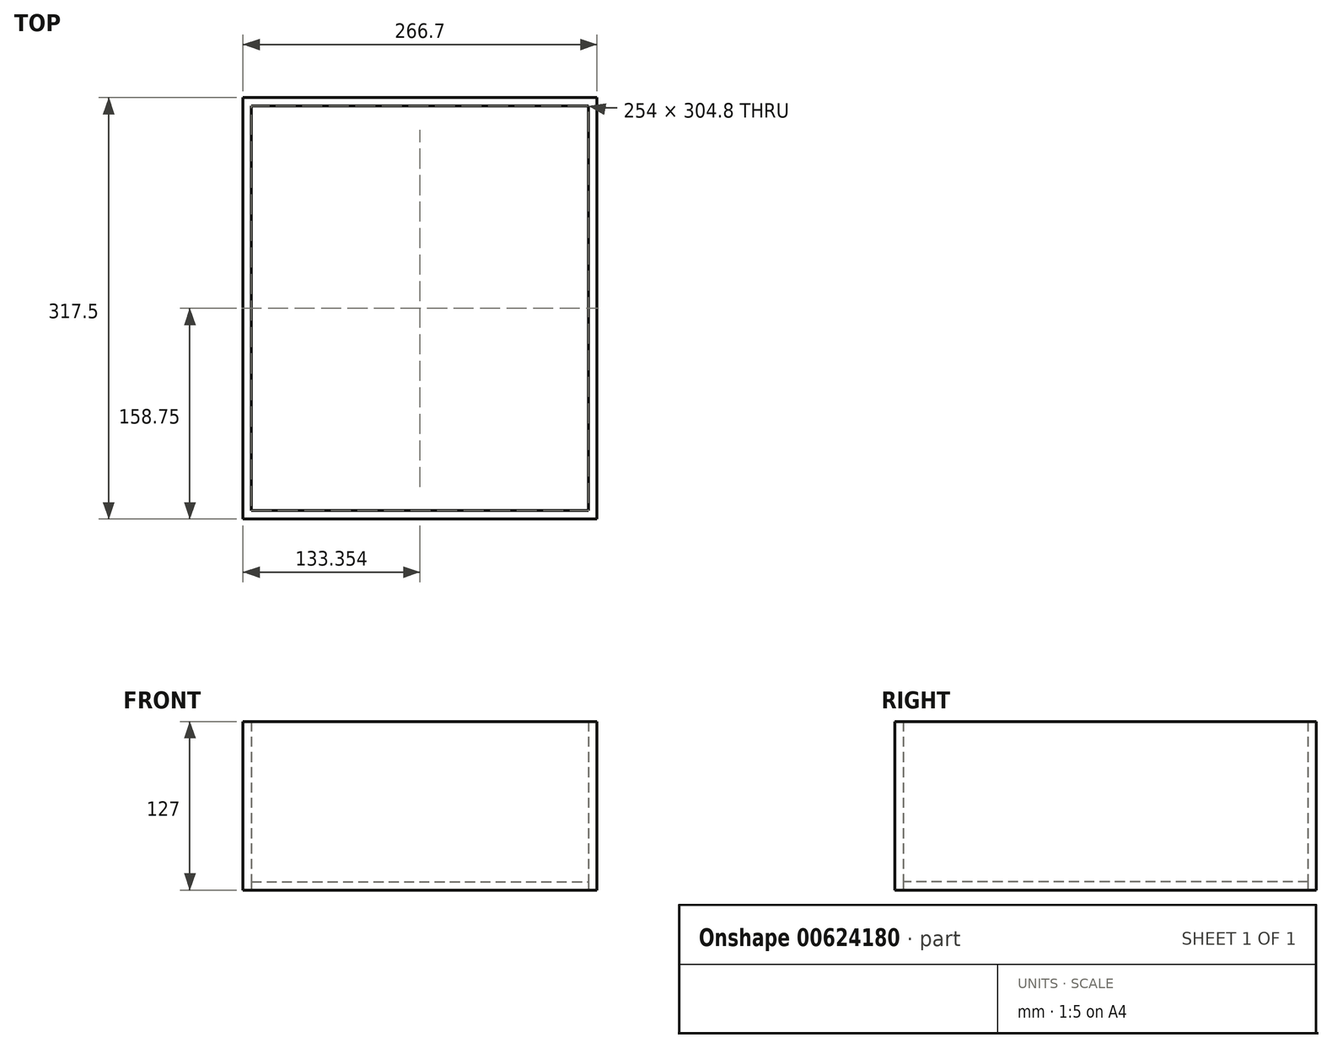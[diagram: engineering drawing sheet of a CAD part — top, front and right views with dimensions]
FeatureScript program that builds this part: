
annotation { "Feature Type Name" : "Feature", "Feature Type Description" : "" }
export const myFeature = defineFeature(function(context is Context, id is Id, definition is map)
    precondition{}
    {
        {
            var Q0;
            Q0=qCreatedBy(makeId("Top.planeOp"),FACE);
            var sketch = newSketch(context, id + "F0", { "sketchPlane" : qUnion([Q0])});
            skLineSegment(sketch, "E0.bottom", {"start": v(-126.24, 176.09) * mm, "end": v(127.76, 176.09) * mm});
            skLineSegment(sketch, "E0.top", {"start": v(-126.24, -128.71) * mm, "end": v(127.76, -128.71) * mm});
            skLineSegment(sketch, "E0.left", {"start": v(-126.24, 176.09) * mm, "end": v(-126.24, -128.71) * mm});
            skLineSegment(sketch, "E0.right", {"start": v(127.76, 176.09) * mm, "end": v(127.76, -128.71) * mm});
            skLineSegment(sketch, "E1.0", {"start": v(-132.59, 182.44) * mm, "end": v(134.11, 182.44) * mm});
            skLineSegment(sketch, "E1.1", {"start": v(-132.59, 182.44) * mm, "end": v(-132.59, -135.06) * mm});
            skLineSegment(sketch, "E1.2", {"start": v(-132.59, -135.06) * mm, "end": v(134.11, -135.06) * mm});
            skLineSegment(sketch, "E1.3", {"start": v(134.11, 182.44) * mm, "end": v(134.11, -135.06) * mm});
            skSolve(sketch);
        }
        {
            var Q0;
            Q0=makeQuery(id+"F0.imprint","IMPRINT",FACE,{"disambiguationData":[TD([[makeQuery(id+"F0.imprint","IMPRINT",EDGE,{"derivedFrom":sQuery(id+"F0.wireOp",EDGE,"E0.bottom")}),-1.0]])]});
            extrude(context, id + "F1", {"entities" : qUnion([Q0]), "depth" : 6.35 * mm, "offsetDistance" : 25.4 * mm});
        }
        {
            var Q0;
            Q0 = qSketchRegion(id + "F0", true);
            extrude(context, id + "F2", {"entities" : qUnion([Q0]), "depth" : 127 * mm, "offsetDistance" : 25.4 * mm});
        }
    });
